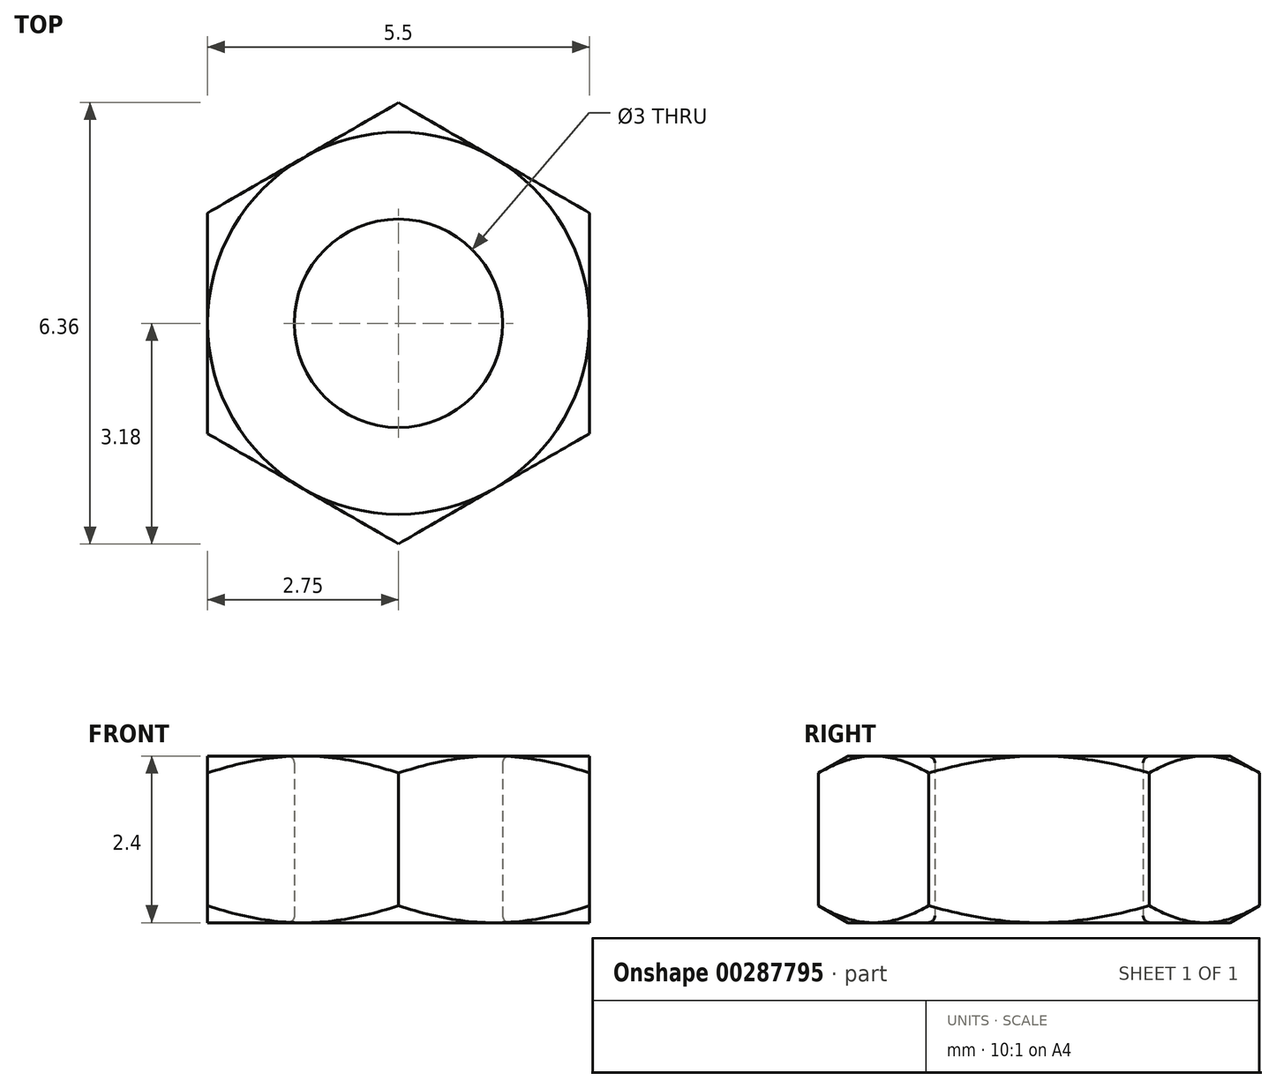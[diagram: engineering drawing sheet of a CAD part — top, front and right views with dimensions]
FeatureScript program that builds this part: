
annotation { "Feature Type Name" : "Feature", "Feature Type Description" : "" }
export const myFeature = defineFeature(function(context is Context, id is Id, definition is map)
    precondition{}
    {
        {
            var Q0;
            Q0=qCreatedBy(makeId("Top.planeOp"),FACE);
            var sketch = newSketch(context, id + "F0", { "sketchPlane" : qUnion([Q0])});
            skCircle(sketch, "E0.cCircle", {"center": v(0, 0) * mm, "radius": 2.75 * mm, "construction": true});
            skLineSegment(sketch, "E0.0", {"start": v(0, -3.18) * mm, "end": v(-2.75, -1.59) * mm});
            skLineSegment(sketch, "E0.1", {"start": v(-2.75, -1.59) * mm, "end": v(-2.75, 1.59) * mm});
            skLineSegment(sketch, "E0.2", {"start": v(-2.75, 1.59) * mm, "end": v(0, 3.18) * mm});
            skLineSegment(sketch, "E0.3", {"start": v(0, 3.18) * mm, "end": v(2.75, 1.59) * mm});
            skLineSegment(sketch, "E0.4", {"start": v(2.75, 1.59) * mm, "end": v(2.75, -1.59) * mm});
            skLineSegment(sketch, "E0.5", {"start": v(2.75, -1.59) * mm, "end": v(0, -3.18) * mm});
            skPoint(sketch, "E0.0.midPoint", {"position": v(-1.38, -2.38) * mm});
            skCircle(sketch, "E1", {"center": v(0, 0) * mm, "radius": 1.5 * mm});
            skSolve(sketch);
        }
        {
            var Q0;
            Q0=qSketchRegion(id+"F0",true);
            extrude(context, id + "F1", {"entities" : qUnion([Q0]), "depth" : 2.4 * mm});
        }
        {
            var Q0;
            Q0=qCreatedBy(makeId("Front.planeOp"),FACE);
            var sketch = newSketch(context, id + "F2", { "sketchPlane" : qUnion([Q0])});
            skLineSegment(sketch, "E2", {"start": v(0, 0) * mm, "end": v(0, 2.4) * mm, "construction": true});
            skLineSegment(sketch, "E3", {"start": v(0, 1.2) * mm, "end": v(2.75, 1.2) * mm, "construction": true});
            skLineSegment(sketch, "E4", {"start": v(2.75, 2.4) * mm, "end": v(4.61, 2.4) * mm});
            skLineSegment(sketch, "E5", {"start": v(4.61, 2.4) * mm, "end": v(4.61, 1.32) * mm});
            skLineSegment(sketch, "E6", {"start": v(4.61, 1.32) * mm, "end": v(2.75, 2.4) * mm});
            skLineSegment(sketch, "E7.MirrorCS", {"start": v(2.75, 0) * mm, "end": v(4.61, 0) * mm});
            skLineSegment(sketch, "E8.MirrorCS", {"start": v(4.61, 0) * mm, "end": v(4.61, 1.08) * mm});
            skLineSegment(sketch, "E9.MirrorCS", {"start": v(4.61, 1.08) * mm, "end": v(2.75, 0) * mm});
            skSolve(sketch);
        }
        {
            var Q0;
            Q0=qSketchRegion(id+"F2",true);
            var Q1;
            Q1=sQuery(id+"F2.wireOp",EDGE,"E2");
            revolve(context, id + "F3", {"operationType" : NewBodyOperationType.REMOVE, "entities" : qUnion([Q0]), "axis" : qUnion([Q1]), "revolveType" : RevolveType.FULL, "oppositeDirection" : true});
        }
        {
            var Q0;
            Q0=makeQuery(id+"F1.opExtrude","CAP_EDGE",EDGE,{"disambiguationData":[OSD([sQuery(id+"F0.wireOp",EDGE,"E1")])],"isStart":false});
            fillet(context, id + "F4", {"entities" : qUnion([Q0]), "radius" : .1 * mm, "tangentPropagation" : true, "allowEdgeOverflow" : false});
        }
        {
            var Q0;
            Q0=makeQuery(id+"F1.opExtrude","CAP_EDGE",EDGE,{"disambiguationData":[OSD([sQuery(id+"F0.wireOp",EDGE,"E1")])],"isStart":true});
            fillet(context, id + "F5", {"entities" : qUnion([Q0]), "radius" : .1 * mm, "tangentPropagation" : true, "allowEdgeOverflow" : false});
        }
    });
